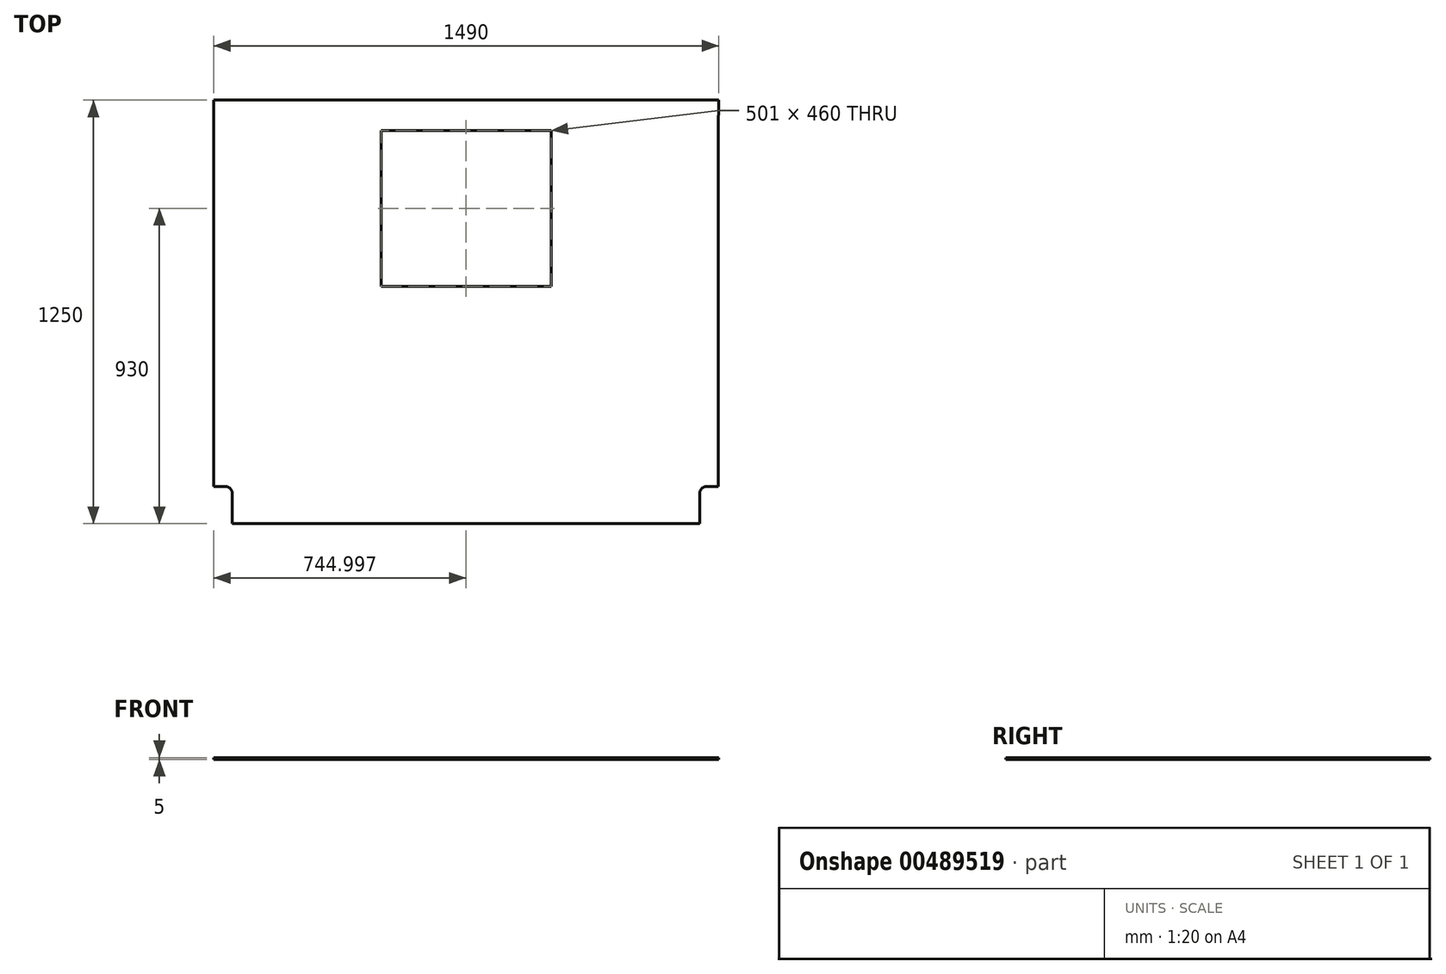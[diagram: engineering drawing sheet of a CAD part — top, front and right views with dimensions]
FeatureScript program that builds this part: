
annotation { "Feature Type Name" : "Feature", "Feature Type Description" : "" }
export const myFeature = defineFeature(function(context is Context, id is Id, definition is map)
    precondition{}
    {
        {
            var Q0;
            Q0=qCreatedBy(makeId("Top.planeOp"),FACE);
            var sketch = newSketch(context, id + "F0", { "sketchPlane" : qUnion([Q0])});
            skLineSegment(sketch, "E0", {"start": v(763.35, 473) * mm, "end": v(763.35, -577) * mm});
            skLineSegment(sketch, "E1", {"start": v(763.35, -577) * mm, "end": v(728.35, -577) * mm});
            skLineSegment(sketch, "E2", {"start": v(-725.96, 473) * mm, "end": v(-725.96, -577) * mm});
            skLineSegment(sketch, "E3", {"start": v(-725.96, -577) * mm, "end": v(-690.96, -577) * mm});
            skLineSegment(sketch, "E4", {"start": v(-670.96, -597) * mm, "end": v(-670.96, -687) * mm});
            skLineSegment(sketch, "E5", {"start": v(-670.96, -687) * mm, "end": v(708.35, -687) * mm});
            skLineSegment(sketch, "E6", {"start": v(708.35, -687) * mm, "end": v(708.35, -597) * mm});
            skLineSegment(sketch, "E7.bottom", {"start": v(-231.46, 472.99) * mm, "end": v(269.54, 472.99) * mm});
            skLineSegment(sketch, "E7.top", {"start": v(-231.46, 12.99) * mm, "end": v(269.54, 12.99) * mm});
            skLineSegment(sketch, "E7.left", {"start": v(-231.46, 472.99) * mm, "end": v(-231.46, 12.99) * mm});
            skLineSegment(sketch, "E7.right", {"start": v(269.54, 472.99) * mm, "end": v(269.54, 12.99) * mm});
            skLineSegment(sketch, "E8", {"start": v(763.35, 473) * mm, "end": v(-725.96, 473) * mm, "construction": true});
            skLineSegment(sketch, "E9", {"start": v(-725.96, 473) * mm, "end": v(-725.96, 562.99) * mm});
            skLineSegment(sketch, "E10", {"start": v(-725.96, 562.99) * mm, "end": v(764.04, 562.99) * mm});
            skLineSegment(sketch, "E11", {"start": v(764.04, 562.99) * mm, "end": v(763.35, 473) * mm});
            skPoint(sketch, "E12.visualSharp", {"position": v(-670.96, -577) * mm});
            skArc(sketch, "E12.filletArc", {"start": v(-670.96, -597) * mm, "mid": v(-676.82, -582.87) * mm, "end": v(-690.96, -577) * mm});
            skPoint(sketch, "E13.visualSharp", {"position": v(708.35, -577) * mm});
            skArc(sketch, "E13.filletArc", {"start": v(728.35, -577) * mm, "mid": v(714.2, -582.87) * mm, "end": v(708.35, -597) * mm});
            skSolve(sketch);
        }
        {
            var Q0;
            Q0=makeQuery(id+"F0.imprint","IMPRINT",FACE,{"disambiguationData":[TD([[makeQuery(id+"F0.imprint","IMPRINT",EDGE,{"derivedFrom":sQuery(id+"F0.wireOp",EDGE,"E0")}),-1.0]])]});
            extrude(context, id + "F1", {"entities" : qUnion([Q0]), "flatOperationType" : FlatOperationType.REMOVE, "offsetDistance" : 25 * mm, "depth" : 5 * mm, "domain" : OperationDomain.MODEL});
        }
    });
